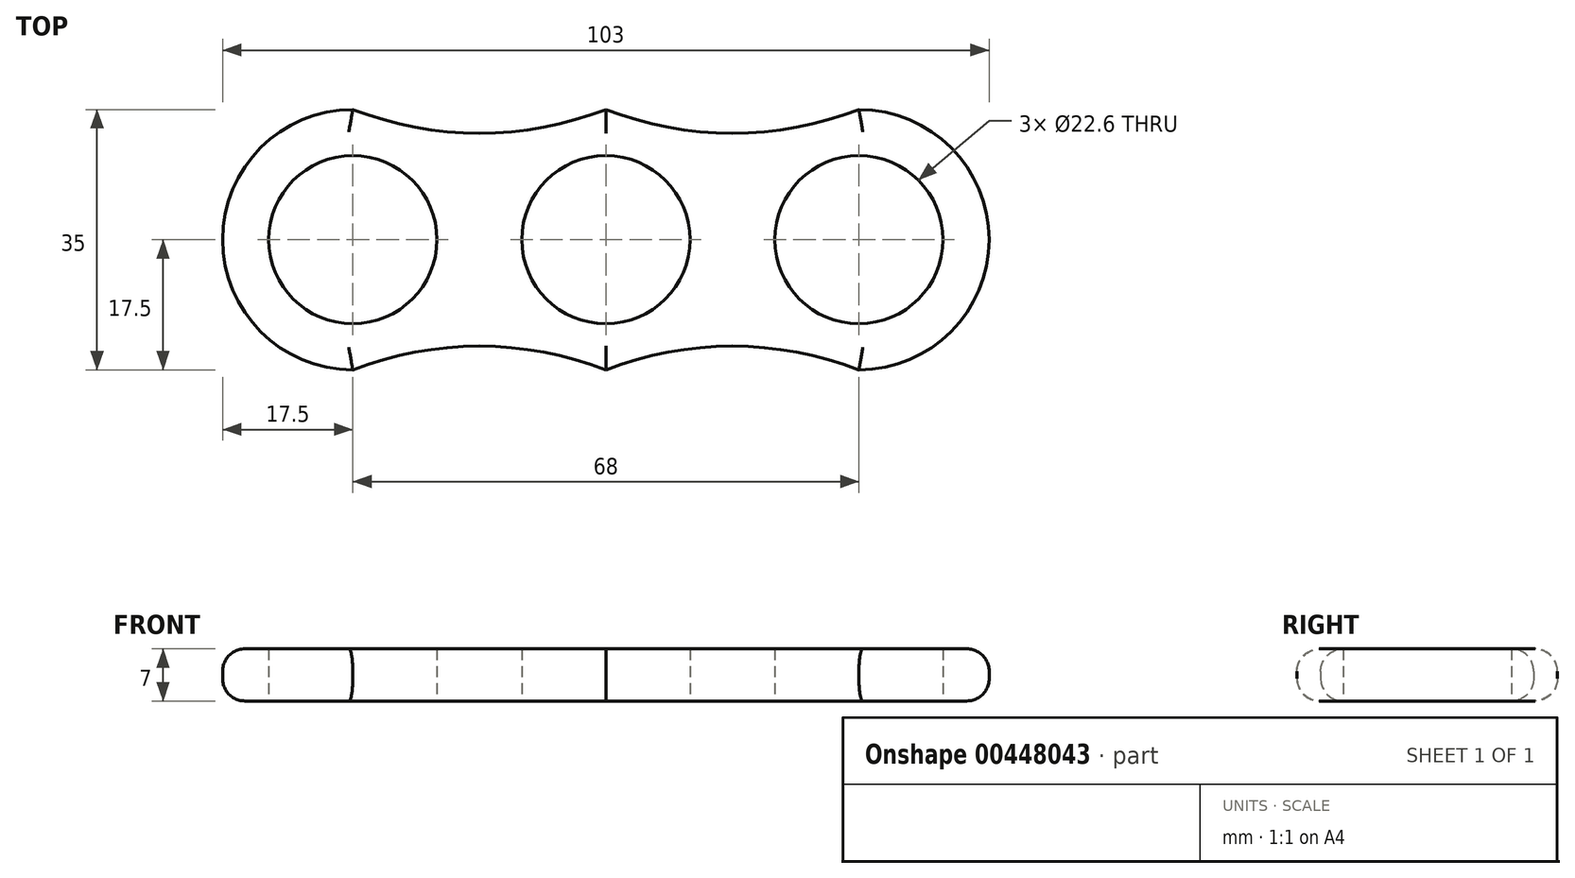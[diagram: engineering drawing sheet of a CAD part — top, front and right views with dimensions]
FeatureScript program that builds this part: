
annotation { "Feature Type Name" : "Feature", "Feature Type Description" : "" }
export const myFeature = defineFeature(function(context is Context, id is Id, definition is map)
    precondition{}
    {
        {
            var Q0;
            Q0=qCreatedBy(makeId("Top.planeOp"),FACE);
            var sketch = newSketch(context, id + "F0", { "sketchPlane" : qUnion([Q0])});
            skCircle(sketch, "E0", {"center": v(0, 0) * mm, "radius": 11.3 * mm});
            skCircle(sketch, "E1", {"center": v(0, 0) * mm, "radius": 17.5 * mm});
            skCircle(sketch, "E2", {"center": v(34, 0) * mm, "radius": 17.5 * mm});
            skCircle(sketch, "E3", {"center": v(-34, 0) * mm, "radius": 17.5 * mm});
            skArc(sketch, "E4", {"start": v(0, 17.5) * mm, "mid": v(17, 14.3) * mm, "end": v(34, 17.5) * mm});
            skArc(sketch, "E5", {"start": v(34, -17.5) * mm, "mid": v(17, -14.3) * mm, "end": v(0, -17.5) * mm});
            skArc(sketch, "E6", {"start": v(-34, 17.5) * mm, "mid": v(-17, 14.3) * mm, "end": v(0, 17.5) * mm});
            skArc(sketch, "E7", {"start": v(0, -17.5) * mm, "mid": v(-17, -14.3) * mm, "end": v(-34, -17.5) * mm});
            skCircle(sketch, "E8", {"center": v(-34, 0) * mm, "radius": 11.3 * mm});
            skCircle(sketch, "E9", {"center": v(34, 0) * mm, "radius": 11.3 * mm});
            skSolve(sketch);
        }
        {
            var Q0;
            Q0=makeQuery(id+"F0.imprint","IMPRINT",FACE,{"disambiguationData":[TD([[makeQuery(id+"F0.imprint","IMPRINT",EDGE,{"derivedFrom":sQuery(id+"F0.wireOp",EDGE,"E8")}),-1.0]])]});
            var Q1;
            {var subQ0=sQuery(id+"F0.wireOp",EDGE,"E6");var subQ1=sQuery(id+"F0.wireOp",EDGE,"E1");var subQ2=makeQuery(id+"F0.imprint","INTERSECT",VERTEX,{"derivedFrom":[subQ1,subQ0]});Q1=makeQuery(id+"F0.imprint","IMPRINT",FACE,{"disambiguationData":[TD([[makeQuery(id+"F0.imprint","IMPRINT",EDGE,{"disambiguationData":[TD([[subQ2,-1.0]])],"derivedFrom":subQ1}),-1.0]])]});}
            var Q2;
            {var subQ0=sQuery(id+"F0.wireOp",EDGE,"E3");var subQ1=sQuery(id+"F0.wireOp",EDGE,"E1");var subQ2=makeQuery(id+"F0.imprint","INTERSECT",VERTEX,{"disambiguationData":[OD(0.0)],"derivedFrom":[subQ1,subQ0]});Q2=makeQuery(id+"F0.imprint","IMPRINT",FACE,{"disambiguationData":[TD([[makeQuery(id+"F0.imprint","IMPRINT",EDGE,{"disambiguationData":[TD([[subQ2,-1.0]])],"derivedFrom":subQ1}),1.0]])]});}
            var Q3;
            {var subQ0=sQuery(id+"F0.wireOp",EDGE,"E7");var subQ1=sQuery(id+"F0.wireOp",EDGE,"E1");var subQ2=makeQuery(id+"F0.imprint","INTERSECT",VERTEX,{"derivedFrom":[subQ1,subQ0]});Q3=makeQuery(id+"F0.imprint","IMPRINT",FACE,{"disambiguationData":[TD([[makeQuery(id+"F0.imprint","IMPRINT",EDGE,{"disambiguationData":[TD([[subQ2,1.0]])],"derivedFrom":subQ1}),-1.0]])]});}
            var Q4;
            Q4=makeQuery(id+"F0.imprint","IMPRINT",FACE,{"disambiguationData":[TD([[makeQuery(id+"F0.imprint","IMPRINT",EDGE,{"derivedFrom":sQuery(id+"F0.wireOp",EDGE,"E0")}),-1.0]])]});
            var Q5;
            {var subQ0=sQuery(id+"F0.wireOp",EDGE,"E5");var subQ1=sQuery(id+"F0.wireOp",EDGE,"E1");var subQ2=makeQuery(id+"F0.imprint","INTERSECT",VERTEX,{"derivedFrom":[subQ1,subQ0]});Q5=makeQuery(id+"F0.imprint","IMPRINT",FACE,{"disambiguationData":[TD([[makeQuery(id+"F0.imprint","IMPRINT",EDGE,{"disambiguationData":[TD([[subQ2,-1.0]])],"derivedFrom":subQ1}),-1.0]])]});}
            var Q6;
            {var subQ0=sQuery(id+"F0.wireOp",EDGE,"E2");var subQ1=sQuery(id+"F0.wireOp",EDGE,"E1");var subQ2=makeQuery(id+"F0.imprint","INTERSECT",VERTEX,{"disambiguationData":[OD(0.0)],"derivedFrom":[subQ1,subQ0]});Q6=makeQuery(id+"F0.imprint","IMPRINT",FACE,{"disambiguationData":[TD([[makeQuery(id+"F0.imprint","IMPRINT",EDGE,{"disambiguationData":[TD([[subQ2,1.0]])],"derivedFrom":subQ1}),1.0]])]});}
            var Q7;
            {var subQ0=sQuery(id+"F0.wireOp",EDGE,"E4");var subQ1=sQuery(id+"F0.wireOp",EDGE,"E1");var subQ2=makeQuery(id+"F0.imprint","INTERSECT",VERTEX,{"derivedFrom":[subQ1,subQ0]});Q7=makeQuery(id+"F0.imprint","IMPRINT",FACE,{"disambiguationData":[TD([[makeQuery(id+"F0.imprint","IMPRINT",EDGE,{"disambiguationData":[TD([[subQ2,1.0]])],"derivedFrom":subQ1}),-1.0]])]});}
            var Q8;
            Q8=makeQuery(id+"F0.imprint","IMPRINT",FACE,{"disambiguationData":[TD([[makeQuery(id+"F0.imprint","IMPRINT",EDGE,{"derivedFrom":sQuery(id+"F0.wireOp",EDGE,"E9")}),-1.0]])]});
            extrude(context, id + "F1", {"entities" : qUnion([Q0, Q1, Q2, Q3, Q4, Q5, Q6, Q7, Q8]), "depth" : 7 * mm});
        }
        {
            var Q0;
            Q0=makeQuery(id+"F1.opExtrude","CAP_EDGE",EDGE,{"disambiguationData":[OSD([sQuery(id+"F0.wireOp",EDGE,"E7")])],"isStart":false});
            var Q1;
            Q1=makeQuery(id+"F1.opExtrude","CAP_EDGE",EDGE,{"disambiguationData":[OSD([sQuery(id+"F0.wireOp",EDGE,"E3")])],"isStart":false});
            var Q2;
            Q2=makeQuery(id+"F1.opExtrude","CAP_EDGE",EDGE,{"disambiguationData":[OSD([sQuery(id+"F0.wireOp",EDGE,"E6")])],"isStart":false});
            var Q3;
            Q3=makeQuery(id+"F1.opExtrude","CAP_EDGE",EDGE,{"disambiguationData":[OSD([sQuery(id+"F0.wireOp",EDGE,"E4")])],"isStart":false});
            var Q4;
            Q4=makeQuery(id+"F1.opExtrude","CAP_EDGE",EDGE,{"disambiguationData":[OSD([sQuery(id+"F0.wireOp",EDGE,"E2")])],"isStart":false});
            var Q5;
            Q5=makeQuery(id+"F1.opExtrude","CAP_EDGE",EDGE,{"disambiguationData":[OSD([sQuery(id+"F0.wireOp",EDGE,"E5")])],"isStart":false});
            fillet(context, id + "F2", {"entities" : qUnion([Q0, Q1, Q2, Q3, Q4, Q5]), "radius" : 3 * mm, "tangentPropagation" : true, "allowEdgeOverflow" : false});
        }
        {
            var Q0;
            Q0=makeQuery(id+"F1.opExtrude","CAP_EDGE",EDGE,{"disambiguationData":[OSD([sQuery(id+"F0.wireOp",EDGE,"E7")])],"isStart":true});
            var Q1;
            Q1=makeQuery(id+"F1.opExtrude","CAP_EDGE",EDGE,{"disambiguationData":[OSD([sQuery(id+"F0.wireOp",EDGE,"E3")])],"isStart":true});
            var Q2;
            Q2=makeQuery(id+"F1.opExtrude","CAP_EDGE",EDGE,{"disambiguationData":[OSD([sQuery(id+"F0.wireOp",EDGE,"E6")])],"isStart":true});
            var Q3;
            Q3=makeQuery(id+"F1.opExtrude","CAP_EDGE",EDGE,{"disambiguationData":[OSD([sQuery(id+"F0.wireOp",EDGE,"E4")])],"isStart":true});
            var Q4;
            Q4=makeQuery(id+"F1.opExtrude","CAP_EDGE",EDGE,{"disambiguationData":[OSD([sQuery(id+"F0.wireOp",EDGE,"E5")])],"isStart":true});
            var Q5;
            Q5=makeQuery(id+"F1.opExtrude","CAP_EDGE",EDGE,{"disambiguationData":[OSD([sQuery(id+"F0.wireOp",EDGE,"E2")])],"isStart":true});
            fillet(context, id + "F3", {"entities" : qUnion([Q0, Q1, Q2, Q3, Q4, Q5]), "radius" : 3 * mm, "tangentPropagation" : true, "allowEdgeOverflow" : false});
        }
    });
